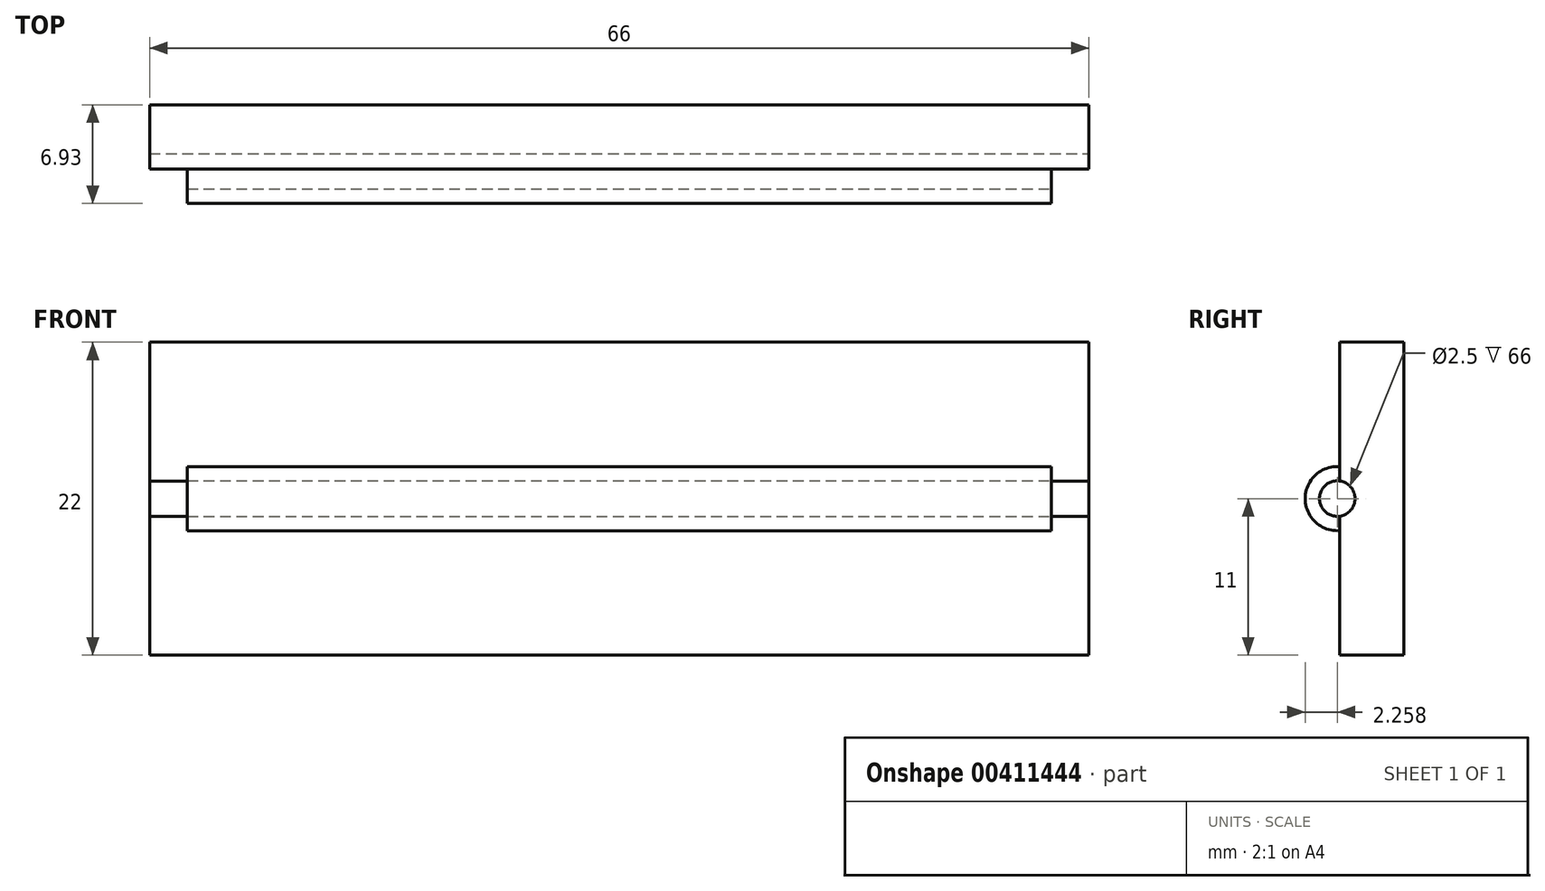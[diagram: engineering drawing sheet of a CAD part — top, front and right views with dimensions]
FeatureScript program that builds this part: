
annotation { "Feature Type Name" : "Feature", "Feature Type Description" : "" }
export const myFeature = defineFeature(function(context is Context, id is Id, definition is map)
    precondition{}
    {
        {
            var Q0;
            Q0=qCreatedBy(makeId("Front.planeOp"),FACE);
            var sketch = newSketch(context, id + "F0", { "sketchPlane" : qUnion([Q0])});
            skLineSegment(sketch, "E0.bottom", {"start": v(33, -11) * mm, "end": v(-33, -11) * mm});
            skLineSegment(sketch, "E0.top", {"start": v(33, 11) * mm, "end": v(-33, 11) * mm});
            skLineSegment(sketch, "E0.left", {"start": v(33, -11) * mm, "end": v(33, 11) * mm});
            skLineSegment(sketch, "E0.right", {"start": v(-33, -11) * mm, "end": v(-33, 11) * mm});
            skPoint(sketch, "E0.middle", {"position": v(0, 0) * mm});
            skLineSegment(sketch, "E1.bottom", {"start": v(-33, 11) * mm, "end": v(-30.35, 11) * mm});
            skLineSegment(sketch, "E1.top", {"start": v(-33, -11) * mm, "end": v(-30.35, -11) * mm});
            skLineSegment(sketch, "E1.left", {"start": v(-33, 11) * mm, "end": v(-33, -11) * mm});
            skLineSegment(sketch, "E1.right", {"start": v(-30.35, 11) * mm, "end": v(-30.35, -11) * mm});
            skLineSegment(sketch, "E2.bottom", {"start": v(33, 11) * mm, "end": v(30.35, 11) * mm});
            skLineSegment(sketch, "E2.top", {"start": v(33, -11) * mm, "end": v(30.35, -11) * mm});
            skLineSegment(sketch, "E2.left", {"start": v(33, 11) * mm, "end": v(33, -11) * mm});
            skLineSegment(sketch, "E2.right", {"start": v(30.35, 11) * mm, "end": v(30.35, -11) * mm});
            skSolve(sketch);
        }
        {
            var Q0;
            Q0=makeQuery(id+"F0.imprint","IMPRINT",FACE,{"disambiguationData":[TD([[makeQuery(id+"F0.imprint","IMPRINT",EDGE,{"derivedFrom":sQuery(id+"F0.wireOp",EDGE,"E0.bottom")}),-1.0]])]});
            extrude(context, id + "F1", {"entities" : qUnion([Q0]), "depth" : 2 * mm});
        }
        {
            var Q0;
            Q0=makeQuery(id+"F0.imprint","IMPRINT",FACE,{"disambiguationData":[TD([[makeQuery(id+"F0.imprint","IMPRINT",EDGE,{"derivedFrom":sQuery(id+"F0.wireOp",EDGE,"E2.bottom")}),1.0]])]});
            var Q1;
            Q1=makeQuery(id+"F0.imprint","IMPRINT",FACE,{"disambiguationData":[TD([[makeQuery(id+"F0.imprint","IMPRINT",EDGE,{"derivedFrom":sQuery(id+"F0.wireOp",EDGE,"E0.bottom")}),-1.0]])]});
            var Q2;
            Q2=makeQuery(id+"F0.imprint","IMPRINT",FACE,{"disambiguationData":[TD([[makeQuery(id+"F0.imprint","IMPRINT",EDGE,{"derivedFrom":sQuery(id+"F0.wireOp",EDGE,"E1.bottom")}),-1.0]])]});
            extrude(context, id + "F2", {"entities" : qUnion([Q0, Q1, Q2]), "operationType" : NewBodyOperationType.ADD, "oppositeDirection" : true, "depth" : 2.5 * mm});
        }
        {
            var Q0;
            Q0=qCreatedBy(makeId("Right.planeOp"),FACE);
            var sketch = newSketch(context, id + "F3", { "sketchPlane" : qUnion([Q0])});
            skLineSegment(sketch, "E3", {"start": v(0, 0) * mm, "end": v(-15, 0) * mm});
            skCircle(sketch, "E4", {"center": v(-2.17, 0) * mm, "radius": 1.25 * mm});
            skCircle(sketch, "E5", {"center": v(-2.17, 0) * mm, "radius": 2.26 * mm});
            skSolve(sketch);
        }
        {
            var Q0;
            Q0 = qSketchRegion(id + "F3", true);
            var Q1;
            {var subQ0=sQuery(id+"F3.wireOp",EDGE,"E4");var subQ1=sQuery(id+"F3.wireOp",EDGE,"E3");var subQ2=makeQuery(id+"F3.imprint","INTERSECT",VERTEX,{"disambiguationData":[OD(0.0)],"derivedFrom":[subQ1,subQ0]});Q1=makeQuery(id+"F3.imprint","IMPRINT",FACE,{"disambiguationData":[TD([[makeQuery(id+"F3.imprint","IMPRINT",EDGE,{"disambiguationData":[TD([[subQ2,1.0]])],"derivedFrom":subQ1}),-1.0]])]});}
            var Q2;
            {var subQ0=sQuery(id+"F3.wireOp",EDGE,"E4");var subQ1=sQuery(id+"F3.wireOp",EDGE,"E3");var subQ2=makeQuery(id+"F3.imprint","INTERSECT",VERTEX,{"disambiguationData":[OD(0.0)],"derivedFrom":[subQ1,subQ0]});Q2=makeQuery(id+"F3.imprint","IMPRINT",FACE,{"disambiguationData":[TD([[makeQuery(id+"F3.imprint","IMPRINT",EDGE,{"disambiguationData":[TD([[subQ2,1.0]])],"derivedFrom":subQ1}),1.0]])]});}
            var Q3;
            Q3=makeQuery(id+"F1.opExtrude","SWEPT_FACE",FACE,{"disambiguationData":[OSD([sQuery(id+"F0.wireOp",EDGE,"E1.right")])]});
            extrude(context, id + "F4", {"entities" : qUnion([Q0, Q1, Q2, Q3]), "operationType" : NewBodyOperationType.ADD, "depth" : (60.7 / 2) * mm});
        }
        {
            var Q0;
            Q0 = qSketchRegion(id + "F3", true);
            extrude(context, id + "F5", {"entities" : qUnion([Q0]), "operationType" : NewBodyOperationType.ADD, "oppositeDirection" : true, "depth" : (60.7 / 2) * mm});
        }
        {
            var Q0;
            Q0=sQuery(id+"F3.wireOp",VERTEX,"E5.center");
            var Q1;
            Q1=makeQuery(id+"F1.opExtrude","SWEPT_BODY",BODY,{"disambiguationData":[OSD([sQuery(id+"F0.wireOp",EDGE,"E0.bottom"),sQuery(id+"F0.wireOp",EDGE,"E0.top"),sQuery(id+"F0.wireOp",EDGE,"E1.right"),sQuery(id+"F0.wireOp",EDGE,"E2.right")])]});
            hole(context, id + "F6", {"style" : HoleStyle.SIMPLE, "endStyle" : HoleEndStyle.THROUGH, "holeDiameter" : 2.5 * mm, "isTappedThrough" : true, "tappedDepth" : 12 * mm, "tapClearance" : 3, "startFromSketch" : true, "locations" : qUnion([Q0]), "scope" : qUnion([Q1])});
        }
        {
            var Q0;
            Q0=sQuery(id+"F3.wireOp",VERTEX,"E5.center");
            var Q1;
            Q1=makeQuery(id+"F1.opExtrude","SWEPT_BODY",BODY,{"disambiguationData":[OSD([sQuery(id+"F0.wireOp",EDGE,"E0.bottom"),sQuery(id+"F0.wireOp",EDGE,"E0.top"),sQuery(id+"F0.wireOp",EDGE,"E1.right"),sQuery(id+"F0.wireOp",EDGE,"E2.right")])]});
            hole(context, id + "F7", {"style" : HoleStyle.SIMPLE, "endStyle" : HoleEndStyle.THROUGH, "oppositeDirection" : true, "holeDiameter" : 2.5 * mm, "isTappedThrough" : true, "tappedDepth" : 12 * mm, "tapClearance" : 3, "startFromSketch" : true, "locations" : qUnion([Q0]), "scope" : qUnion([Q1])});
        }
    });
